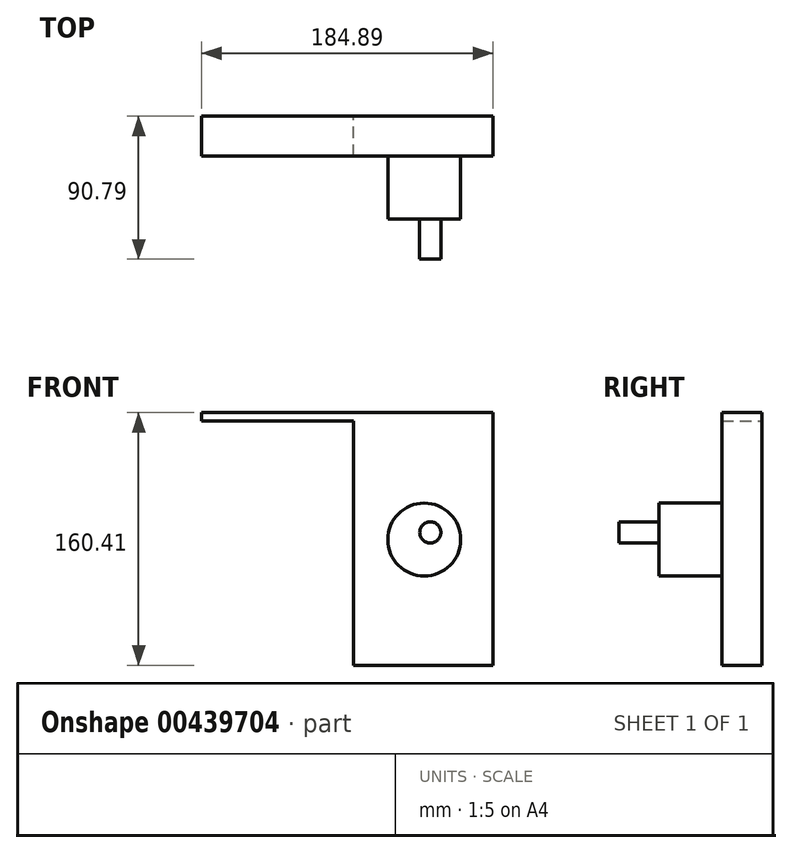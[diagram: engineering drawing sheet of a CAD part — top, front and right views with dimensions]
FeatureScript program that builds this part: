
annotation { "Feature Type Name" : "Feature", "Feature Type Description" : "" }
export const myFeature = defineFeature(function(context is Context, id is Id, definition is map)
    precondition{}
    {
        {
            var Q0;
            Q0=qCreatedBy(makeId("Front.planeOp"),FACE);
            var sketch = newSketch(context, id + "F0", { "sketchPlane" : qUnion([Q0])});
            skLineSegment(sketch, "E0.bottom", {"start": v(-96.46, 95.8) * mm, "end": v(88.43, 95.8) * mm});
            skLineSegment(sketch, "E0.top", {"start": v(-96.46, 101.1) * mm, "end": v(88.43, 101.1) * mm});
            skLineSegment(sketch, "E0.left", {"start": v(-96.46, 95.8) * mm, "end": v(-96.46, 101.1) * mm});
            skLineSegment(sketch, "E0.right", {"start": v(88.43, 95.8) * mm, "end": v(88.43, 101.1) * mm});
            skLineSegment(sketch, "E1.bottom", {"start": v(88.43, 101.1) * mm, "end": v(0, 101.1) * mm});
            skLineSegment(sketch, "E1.top", {"start": v(88.43, -59.3) * mm, "end": v(0, -59.3) * mm});
            skLineSegment(sketch, "E1.left", {"start": v(88.43, 101.1) * mm, "end": v(88.43, -59.3) * mm});
            skLineSegment(sketch, "E1.right", {"start": v(0, 101.1) * mm, "end": v(0, -59.3) * mm});
            skSolve(sketch);
        }
        {
            var Q0;
            Q0 = qSketchRegion(id + "F0", true);
            extrude(context, id + "F1", {"entities" : qUnion([Q0]), "depth" : 25.4 * mm});
        }
        {
            var Q0;
            Q0=qCreatedBy(makeId("Front.planeOp"),FACE);
            var sketch = newSketch(context, id + "F2", { "sketchPlane" : qUnion([Q0])});
            skCircle(sketch, "E2", {"center": v(44.85, 20.54) * mm, "radius": 23.15 * mm});
            skSolve(sketch);
        }
        {
            var Q0;
            Q0=makeQuery(id+"F2.imprint","IMPRINT",FACE,{"disambiguationData":[TD([[makeQuery(id+"F2.imprint","IMPRINT",EDGE,{"derivedFrom":sQuery(id+"F2.wireOp",EDGE,"E2")}),1.0]])]});
            extrude(context, id + "F3", {"entities" : qUnion([Q0]), "operationType" : NewBodyOperationType.ADD, "depth" : 65.4 * mm});
        }
        {
            var Q0;
            Q0=makeQuery(id+"F3.opExtrude","CAP_FACE",FACE,{"disambiguationData":[OSD([sQuery(id+"F2.wireOp",EDGE,"E2")])],"isStart":false});
            var sketch = newSketch(context, id + "F4", { "sketchPlane" : qUnion([Q0])});
            skCircle(sketch, "E3", {"center": v(48.74, 25.05) * mm, "radius": 6.73 * mm});
            skSolve(sketch);
        }
        {
            var Q0;
            Q0 = qSketchRegion(id + "F4", true);
            extrude(context, id + "F5", {"entities" : qUnion([Q0]), "operationType" : NewBodyOperationType.ADD, "depth" : 25.4 * mm});
        }
    });
